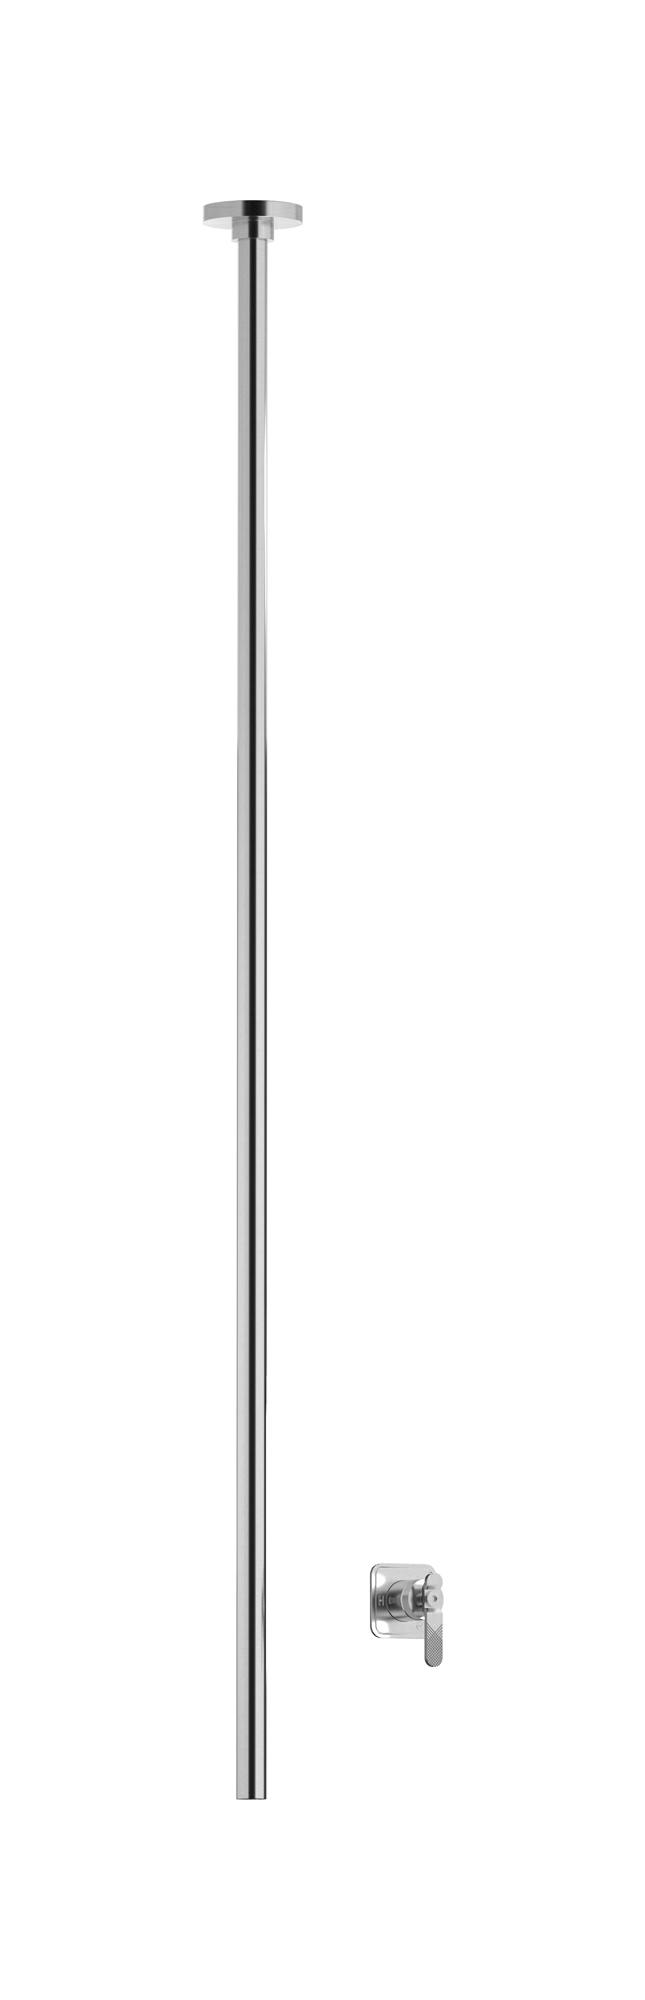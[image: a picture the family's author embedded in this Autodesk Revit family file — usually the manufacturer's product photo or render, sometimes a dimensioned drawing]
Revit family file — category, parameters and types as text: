
# Revit family: B2210
name_source: partatom
category: Apparecchi idraulici
units: mm (PartAtom-declared; Revit-internal decimal feet)

## family parameters
Basato su piano di lavoro = No
Condiviso = No
Mantieni orientamento annotazione = No
Numero OmniClass = 23.45.55.17
Punto di calcolo locali = No
Quota connettore circolare = Usa diametro
Sempre verticale = Sì
Taglio con vuoti quando caricato = No
Tipo di parte = Normale
Titolo OmniClass = Mixing Faucets

## types (13) — shared parameters
Cold water inlet = 10 mm  [stored 0.0328084 ft]
Commenti sul tipo = Ceiling spout with wall mounted mixer
Connessione CW = No
Connessione HW = No
Connessione di scarico = No
Connessione di ventilazione = No
Descrizione = Ceiling spout with wall mounted mixer
Hot water inlet = 10 mm  [stored 0.0328084 ft]
Produttore = IB Rubinetterie S.p.A.
URL = https://www.weareib.it
zero-valued in all types: Prospetto di default

## per-type parameters (varying)
| type | Finishes surface | Immagine tipo | Modello |
| Chrome | IB_Chrome | B2210CC.jpg | B2210CC |
| Black Chrome | IB_Black chrome | B2210CF.jpg | B2210CF |
| Brushed Black Chrome | IB_Brushed black chrome | B2210CS.jpg | B2210CS |
| Pale Gold | IB_Pale gold | B2210II.jpg | B2210II |
| Brushed Pale Gold | IB_brushed pale gold | B2210IS.jpg | B2210IS |
| Modern Bronze | IB_Modern bronze | B2210MB.jpg | B2210MB |
| Matt Black | IB_matt black | B2210NP.jpg | B2210NP |
| Natural Brass | IB_Brass | B2210ON.jpg | B2210ON |
| Gold | IB_gold | B2210OO.jpg | B2210OO |
| Brushed Gold | IB_brushed gold | B2210OS.jpg | B2210OS |
| Rose Gold | IB_Rose gold | B2210RS.jpg | B2210RS |
| Brushed Rose Gold | IB_Brushed rose gold | B2210SR.jpg | B2210SR |
| Brushed Nickel | IB_Brushed nickel | B2210SS.jpg | B2210SS |

note: [stored X ft] marks values corroborated as IEEE doubles in the binary element streams (Revit-internal decimal feet)
